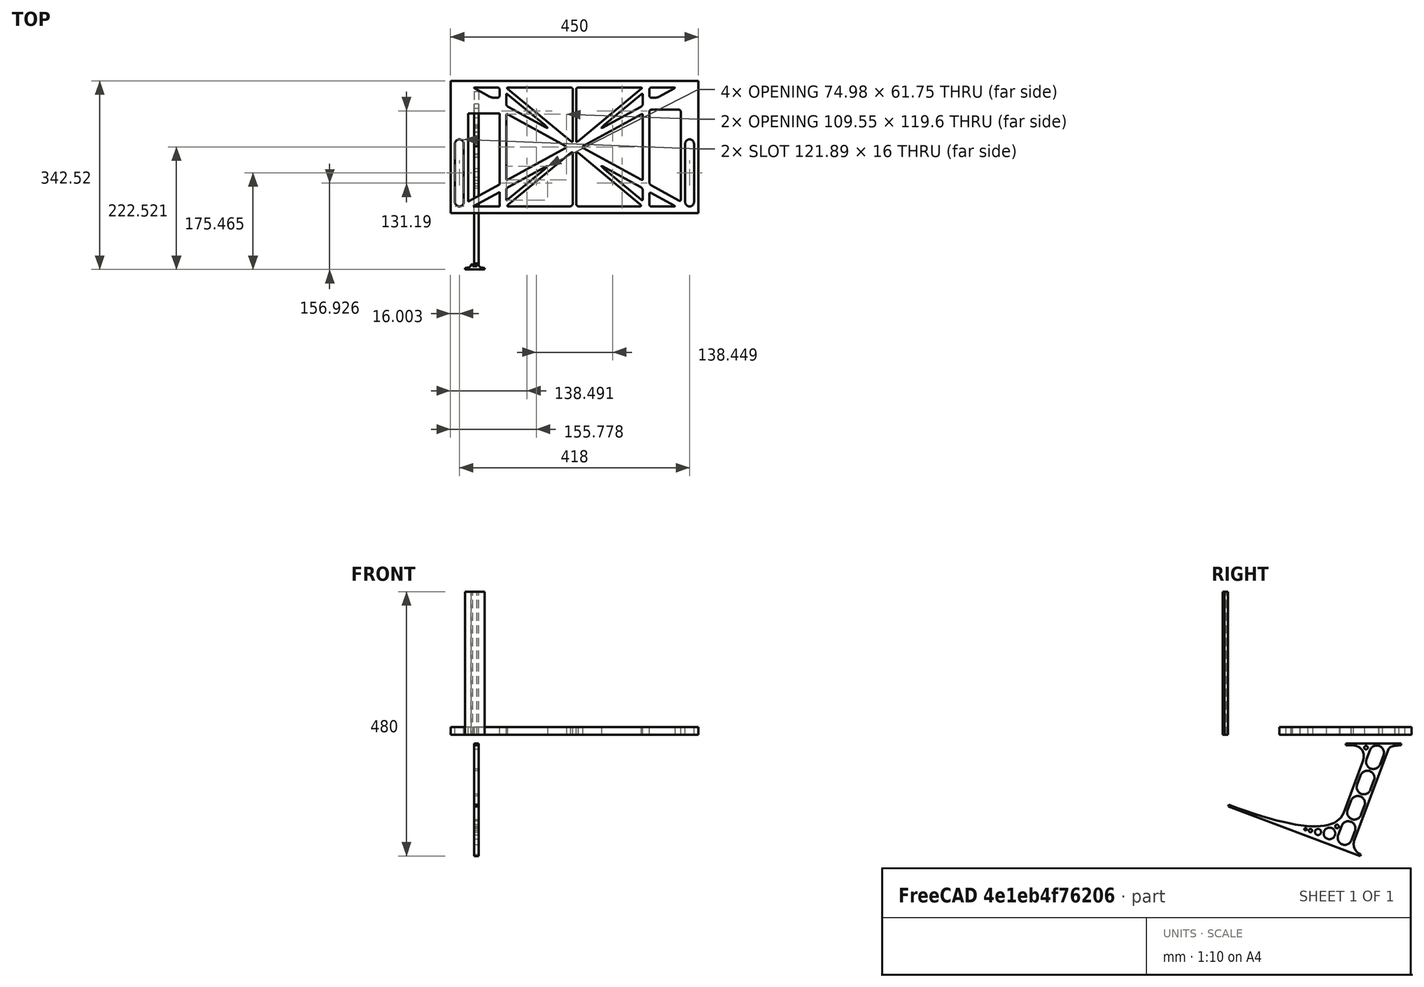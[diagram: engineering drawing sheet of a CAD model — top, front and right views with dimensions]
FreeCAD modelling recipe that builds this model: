
FCSTD DOCUMENT  (FreeCAD 0.19R0.19.2)
Label: laptopStand122FCStd
License: All rights reserved
LicenseURL: http://en.wikipedia.org/wiki/All_rights_reserved
objects: Sketcher::SketchObject×3, Part::Extrusion×3
note: 6 computed .brp shape members not serialized (recipe doc carries the construction recipe); baked Part::Feature solids carry a one-line shape summary decoded from their .brp

FEATURE [Sketcher::SketchObject] Sketch
  FullyConstrained = false
  sketch-geometry (338):
    g0: LineSegment StartX=-10.9272 StartY=-82.7794 StartZ=0 EndX=46.0728 EndY=-51.4823 EndZ=0
    g1: LineSegment StartX=-10.9272 StartY=77.3346 StartZ=0 EndX=-10.9272 EndY=-82.7794 EndZ=0
    g2: LineSegment StartX=46.0728 StartY=-65.424 StartZ=0 EndX=-1.92719 EndY=-91.7794 EndZ=0
    g3: LineSegment StartX=46.0728 StartY=-65.424 StartZ=0 EndX=46.0728 EndY=-91.7794 EndZ=0
    g4: LineSegment StartX=46.0728 StartY=77.3346 StartZ=0 EndX=46.0728 EndY=-51.4823 EndZ=0
    g5: LineSegment StartX=-42.9272 StartY=136.221 StartZ=0 EndX=-42.9272 EndY=-103.779 EndZ=0
    g6: LineSegment StartX=407.073 StartY=136.221 StartZ=0 EndX=407.073 EndY=-103.779 EndZ=0
    g7: ArcOfCircle CenterX=-26.9272 CenterY=22.1087 CenterZ=0 NormalX=0 NormalY=0 NormalZ=1 AngleXU=0 Radius=8 StartAngle=1e-16 EndAngle=3.14159
    g8: ArcOfCircle CenterX=-26.9272 CenterY=-83.7794 CenterZ=0 NormalX=0 NormalY=0 NormalZ=1 AngleXU=0 Radius=8 StartAngle=3.14159 EndAngle=6.28319
    g9: LineSegment StartX=-34.9272 StartY=22.1087 StartZ=0 EndX=-34.9272 EndY=-83.7794 EndZ=0
    g10: LineSegment StartX=-18.9272 StartY=22.1087 StartZ=0 EndX=-18.9272 EndY=-83.7794 EndZ=0
    g11: ArcOfCircle CenterX=391.073 CenterY=22.1087 CenterZ=0 NormalX=0 NormalY=0 NormalZ=1 AngleXU=0 Radius=8 StartAngle=-4.4e-15 EndAngle=3.14159
    g12: LineSegment StartX=399.073 StartY=22.1087 StartZ=0 EndX=399.073 EndY=-83.7794 EndZ=0
    g13: LineSegment StartX=383.073 StartY=22.1087 StartZ=0 EndX=383.073 EndY=-83.7794 EndZ=0
    g14: ArcOfCircle CenterX=391.073 CenterY=-83.7794 CenterZ=0 NormalX=0 NormalY=0 NormalZ=1 AngleXU=0 Radius=8 StartAngle=3.14159 EndAngle=6.28319
    g15: Circle CenterX=175.022 CenterY=27.0628 CenterZ=0 NormalX=0 NormalY=0 NormalZ=1 AngleXU=0 Radius=1
    g16: Circle CenterX=179.022 CenterY=24.8665 CenterZ=0 NormalX=0 NormalY=0 NormalZ=1 AngleXU=0 Radius=1
    g17: Circle CenterX=179.022 CenterY=27.0628 CenterZ=0 NormalX=0 NormalY=0 NormalZ=1 AngleXU=0 Radius=1
    g18: BSplineCurve PolesCount=3 KnotsCount=2 Degree=2 IsPeriodic=0
    g19: GeomPoint X=175.022 Y=27.0628 Z=0
    g20: GeomPoint X=179.022 Y=27.0628 Z=0
    g21: Circle CenterX=189.124 CenterY=27.0628 CenterZ=0 NormalX=0 NormalY=0 NormalZ=1 AngleXU=0 Radius=1
    g22: Circle CenterX=185.124 CenterY=24.8665 CenterZ=0 NormalX=0 NormalY=0 NormalZ=1 AngleXU=0 Radius=1
    g23: Circle CenterX=185.124 CenterY=27.0628 CenterZ=0 NormalX=0 NormalY=0 NormalZ=1 AngleXU=0 Radius=1
    g24: BSplineCurve PolesCount=3 KnotsCount=2 Degree=2 IsPeriodic=0
    g25: GeomPoint X=189.124 Y=27.0628 Z=0
    g26: GeomPoint X=185.124 Y=27.0628 Z=0
    g27: Circle CenterX=175.022 CenterY=5.37834 CenterZ=0 NormalX=0 NormalY=0 NormalZ=1 AngleXU=0 Radius=1
    g28: Circle CenterX=179.022 CenterY=7.57463 CenterZ=0 NormalX=0 NormalY=0 NormalZ=1 AngleXU=0 Radius=1
    g29: Circle CenterX=179.022 CenterY=5.34704 CenterZ=0 NormalX=0 NormalY=0 NormalZ=1 AngleXU=0 Radius=1
    g30: BSplineCurve PolesCount=3 KnotsCount=2 Degree=2 IsPeriodic=0
    g31: GeomPoint X=175.022 Y=5.37834 Z=0
    g32: GeomPoint X=179.022 Y=5.34704 Z=0
    g33: Circle CenterX=189.124 CenterY=5.37834 CenterZ=0 NormalX=0 NormalY=0 NormalZ=1 AngleXU=0 Radius=1
    g34: Circle CenterX=185.124 CenterY=7.57463 CenterZ=0 NormalX=0 NormalY=0 NormalZ=1 AngleXU=0 Radius=1
    g35: Circle CenterX=185.124 CenterY=5.34704 CenterZ=0 NormalX=0 NormalY=0 NormalZ=1 AngleXU=0 Radius=1
    g36: BSplineCurve PolesCount=3 KnotsCount=2 Degree=2 IsPeriodic=0
    g37: GeomPoint X=189.124 Y=5.37834 Z=0
    g38: GeomPoint X=185.124 Y=5.34704 Z=0
    g39: Circle CenterX=165.871 CenterY=18.1458 CenterZ=0 NormalX=0 NormalY=0 NormalZ=1 AngleXU=0 Radius=1
    g40: Circle CenterX=169.377 CenterY=16.2206 CenterZ=0 NormalX=0 NormalY=0 NormalZ=1 AngleXU=0 Radius=1
    g41: Circle CenterX=165.871 CenterY=14.2954 CenterZ=0 NormalX=0 NormalY=0 NormalZ=1 AngleXU=0 Radius=1
    g42: BSplineCurve PolesCount=3 KnotsCount=2 Degree=2 IsPeriodic=0
    g43: GeomPoint X=165.871 Y=18.1458 Z=0
    g44: GeomPoint X=165.871 Y=14.2954 Z=0
    g45: Circle CenterX=198.275 CenterY=18.1458 CenterZ=0 NormalX=0 NormalY=0 NormalZ=1 AngleXU=0 Radius=1
    g46: Circle CenterX=194.768 CenterY=16.2206 CenterZ=0 NormalX=0 NormalY=0 NormalZ=1 AngleXU=0 Radius=1
    g47: Circle CenterX=198.275 CenterY=14.2954 CenterZ=0 NormalX=0 NormalY=0 NormalZ=1 AngleXU=0 Radius=1
    g48: BSplineCurve PolesCount=3 KnotsCount=2 Degree=2 IsPeriodic=0
    g49: GeomPoint X=198.275 Y=18.1458 Z=0
    g50: GeomPoint X=198.275 Y=14.2954 Z=0
    g51: LineSegment StartX=407.073 StartY=-103.779 StartZ=0 EndX=-42.9272 EndY=-103.779 EndZ=0
    g52: LineSegment StartX=407.073 StartY=136.221 StartZ=0 EndX=-42.9272 EndY=136.221 EndZ=0
    g53: LineSegment StartX=46.0728 StartY=77.3346 StartZ=0 EndX=-10.9272 EndY=77.3346 EndZ=0
    g54: Circle CenterX=125.607 CenterY=54.1951 CenterZ=0 NormalX=0 NormalY=0 NormalZ=1 AngleXU=0 Radius=1
    g55: Circle CenterX=139.632 CenterY=46.4944 CenterZ=0 NormalX=0 NormalY=0 NormalZ=1 AngleXU=0 Radius=1
    g56: Circle CenterX=127.326 CenterY=56.7187 CenterZ=0 NormalX=0 NormalY=0 NormalZ=1 AngleXU=0 Radius=1
    g57: BSplineCurve PolesCount=3 KnotsCount=2 Degree=2 IsPeriodic=0
    g58: GeomPoint X=125.607 Y=54.1951 Z=0
    g59: GeomPoint X=127.326 Y=56.7187 Z=0
    g60: Circle CenterX=236.821 CenterY=56.7187 CenterZ=0 NormalX=0 NormalY=0 NormalZ=1 AngleXU=0 Radius=1
    g61: Circle CenterX=224.513 CenterY=46.4944 CenterZ=0 NormalX=0 NormalY=0 NormalZ=1 AngleXU=0 Radius=1
    g62: Circle CenterX=238.538 CenterY=54.1951 CenterZ=0 NormalX=0 NormalY=0 NormalZ=1 AngleXU=0 Radius=1
    g63: BSplineCurve PolesCount=3 KnotsCount=2 Degree=2 IsPeriodic=0
    g64: GeomPoint X=236.821 Y=56.7187 Z=0
    g65: GeomPoint X=238.538 Y=54.1951 Z=0
    g66: Circle CenterX=238.538 CenterY=-21.7539 CenterZ=0 NormalX=0 NormalY=0 NormalZ=1 AngleXU=0 Radius=1
    g67: Circle CenterX=224.513 CenterY=-14.0532 CenterZ=0 NormalX=0 NormalY=0 NormalZ=1 AngleXU=0 Radius=1
    g68: Circle CenterX=236.821 CenterY=-24.2775 CenterZ=0 NormalX=0 NormalY=0 NormalZ=1 AngleXU=0 Radius=1
    g69: BSplineCurve PolesCount=3 KnotsCount=2 Degree=2 IsPeriodic=0
    g70: GeomPoint X=238.538 Y=-21.7539 Z=0
    g71: GeomPoint X=236.821 Y=-24.2775 Z=0
    g72: Circle CenterX=125.607 CenterY=-21.7539 CenterZ=0 NormalX=0 NormalY=0 NormalZ=1 AngleXU=0 Radius=1
    g73: Circle CenterX=139.632 CenterY=-14.0532 CenterZ=0 NormalX=0 NormalY=0 NormalZ=1 AngleXU=0 Radius=1
    g74: Circle CenterX=127.325 CenterY=-24.2775 CenterZ=0 NormalX=0 NormalY=0 NormalZ=1 AngleXU=0 Radius=1
    g75: BSplineCurve PolesCount=3 KnotsCount=2 Degree=2 IsPeriodic=0
    g76: GeomPoint X=125.607 Y=-21.7539 Z=0
    g77: GeomPoint X=127.325 Y=-24.2775 Z=0
    g78: Circle CenterX=302.996 CenterY=111.695 CenterZ=0 NormalX=0 NormalY=0 NormalZ=1 AngleXU=0 Radius=1
    g79: Circle CenterX=306.073 CenterY=114.251 CenterZ=0 NormalX=0 NormalY=0 NormalZ=1 AngleXU=0 Radius=1
    g80: Circle CenterX=306.073 CenterY=110.251 CenterZ=0 NormalX=0 NormalY=0 NormalZ=1 AngleXU=0 Radius=1
    g81: BSplineCurve PolesCount=3 KnotsCount=2 Degree=2 IsPeriodic=0
    g82: GeomPoint X=302.996 Y=111.695 Z=0
    g83: GeomPoint X=306.073 Y=110.251 Z=0
    g84: Circle CenterX=306.073 CenterY=95.2763 CenterZ=0 NormalX=0 NormalY=0 NormalZ=1 AngleXU=0 Radius=1
    g85: Circle CenterX=306.073 CenterY=91.2763 CenterZ=0 NormalX=0 NormalY=0 NormalZ=1 AngleXU=0 Radius=1
    g86: Circle CenterX=302.567 CenterY=89.3511 CenterZ=0 NormalX=0 NormalY=0 NormalZ=1 AngleXU=0 Radius=1
    g87: BSplineCurve PolesCount=3 KnotsCount=2 Degree=2 IsPeriodic=0
    g88: GeomPoint X=306.073 Y=95.2763 Z=0
    g89: GeomPoint X=302.567 Y=89.3511 Z=0
    g90: LineSegment StartX=306.073 StartY=110.251 StartZ=0 EndX=306.073 EndY=95.2763 EndZ=0
    g91: LineSegment StartX=302.996 StartY=111.695 StartZ=0 EndX=236.821 EndY=56.7187 EndZ=0
    g92: LineSegment StartX=238.538 StartY=54.1951 StartZ=0 EndX=302.567 EndY=89.3511 EndZ=0
    g93: Circle CenterX=61.1496 CenterY=111.695 CenterZ=0 NormalX=0 NormalY=0 NormalZ=1 AngleXU=0 Radius=1
    g94: Circle CenterX=58.0728 CenterY=114.251 CenterZ=0 NormalX=0 NormalY=0 NormalZ=1 AngleXU=0 Radius=1
    g95: Circle CenterX=58.0728 CenterY=110.251 CenterZ=0 NormalX=0 NormalY=0 NormalZ=1 AngleXU=0 Radius=1
    g96: BSplineCurve PolesCount=3 KnotsCount=2 Degree=2 IsPeriodic=0
    g97: GeomPoint X=61.1496 Y=111.695 Z=0
    g98: GeomPoint X=58.0728 Y=110.251 Z=0
    g99: Circle CenterX=61.5791 CenterY=89.3511 CenterZ=0 NormalX=0 NormalY=0 NormalZ=1 AngleXU=0 Radius=1
    g100: Circle CenterX=58.0728 CenterY=91.2763 CenterZ=0 NormalX=0 NormalY=0 NormalZ=1 AngleXU=0 Radius=1
    g101: Circle CenterX=58.0728 CenterY=95.2763 CenterZ=0 NormalX=0 NormalY=0 NormalZ=1 AngleXU=0 Radius=1
    g102: BSplineCurve PolesCount=3 KnotsCount=2 Degree=2 IsPeriodic=0
    g103: GeomPoint X=61.5791 Y=89.3511 Z=0
    g104: GeomPoint X=58.0728 Y=95.2763 Z=0
    g105: LineSegment StartX=58.0728 StartY=110.251 StartZ=0 EndX=58.0728 EndY=95.2763 EndZ=0
    g106: LineSegment StartX=61.1496 StartY=111.695 StartZ=0 EndX=127.326 EndY=56.7187 EndZ=0
    g107: LineSegment StartX=125.607 StartY=54.1951 StartZ=0 EndX=61.5791 EndY=89.3511 EndZ=0
    g108: Circle CenterX=61.5791 CenterY=-56.9099 CenterZ=0 NormalX=0 NormalY=0 NormalZ=1 AngleXU=0 Radius=1
    g109: Circle CenterX=58.0728 CenterY=-58.8351 CenterZ=0 NormalX=0 NormalY=0 NormalZ=1 AngleXU=0 Radius=1
    g110: Circle CenterX=58.0728 CenterY=-62.8351 CenterZ=0 NormalX=0 NormalY=0 NormalZ=1 AngleXU=0 Radius=1
    g111: BSplineCurve PolesCount=3 KnotsCount=2 Degree=2 IsPeriodic=0
    g112: GeomPoint X=61.5791 Y=-56.9099 Z=0
    g113: GeomPoint X=58.0728 Y=-62.8351 Z=0
    g114: Circle CenterX=58.0728 CenterY=-77.8102 CenterZ=0 NormalX=0 NormalY=0 NormalZ=1 AngleXU=0 Radius=1
    g115: Circle CenterX=58.0728 CenterY=-81.8102 CenterZ=0 NormalX=0 NormalY=0 NormalZ=1 AngleXU=0 Radius=1
    g116: Circle CenterX=61.1496 CenterY=-79.2541 CenterZ=0 NormalX=0 NormalY=0 NormalZ=1 AngleXU=0 Radius=1
    g117: BSplineCurve PolesCount=3 KnotsCount=2 Degree=2 IsPeriodic=0
    g118: GeomPoint X=58.0728 Y=-77.8102 Z=0
    g119: GeomPoint X=61.1496 Y=-79.2541 Z=0
    g120: LineSegment StartX=58.0728 StartY=-62.8351 StartZ=0 EndX=58.0728 EndY=-77.8102 EndZ=0
    g121: LineSegment StartX=61.1496 StartY=-79.2541 StartZ=0 EndX=127.325 EndY=-24.2775 EndZ=0
    g122: LineSegment StartX=125.607 StartY=-21.7539 StartZ=0 EndX=61.5791 EndY=-56.9099 EndZ=0
    g123: Circle CenterX=302.567 CenterY=-56.9099 CenterZ=0 NormalX=0 NormalY=0 NormalZ=1 AngleXU=0 Radius=1
    g124: Circle CenterX=306.073 CenterY=-58.8351 CenterZ=0 NormalX=0 NormalY=0 NormalZ=1 AngleXU=0 Radius=1
    g125: Circle CenterX=306.073 CenterY=-62.8351 CenterZ=0 NormalX=0 NormalY=0 NormalZ=1 AngleXU=0 Radius=1
    g126: BSplineCurve PolesCount=3 KnotsCount=2 Degree=2 IsPeriodic=0
    g127: GeomPoint X=302.567 Y=-56.9099 Z=0
    g128: GeomPoint X=306.073 Y=-62.8351 Z=0
    g129: Circle CenterX=302.996 CenterY=-79.2541 CenterZ=0 NormalX=0 NormalY=0 NormalZ=1 AngleXU=0 Radius=1
    g130: Circle CenterX=306.073 CenterY=-81.8102 CenterZ=0 NormalX=0 NormalY=0 NormalZ=1 AngleXU=0 Radius=1
    g131: Circle CenterX=306.073 CenterY=-77.8102 CenterZ=0 NormalX=0 NormalY=0 NormalZ=1 AngleXU=0 Radius=1
    g132: BSplineCurve PolesCount=3 KnotsCount=2 Degree=2 IsPeriodic=0
    g133: GeomPoint X=302.996 Y=-79.2541 Z=0
    g134: GeomPoint X=306.073 Y=-77.8102 Z=0
    g135: LineSegment StartX=306.073 StartY=-62.8351 StartZ=0 EndX=306.073 EndY=-77.8102 EndZ=0
    g136: LineSegment StartX=302.996 StartY=-79.2541 StartZ=0 EndX=236.821 EndY=-24.2775 EndZ=0
    g137: LineSegment StartX=238.538 StartY=-21.7539 StartZ=0 EndX=302.567 EndY=-56.9099 EndZ=0
    g138: Circle CenterX=61.6457 CenterY=-88.8112 CenterZ=0 NormalX=0 NormalY=0 NormalZ=1 AngleXU=0 Radius=1
    g139: Circle CenterX=58.0728 CenterY=-91.7794 CenterZ=0 NormalX=0 NormalY=0 NormalZ=1 AngleXU=0 Radius=1
    g140: Circle CenterX=63.9135 CenterY=-91.7794 CenterZ=0 NormalX=0 NormalY=0 NormalZ=1 AngleXU=0 Radius=1
    g141: BSplineCurve PolesCount=3 KnotsCount=2 Degree=2 IsPeriodic=0
    g142: GeomPoint X=61.6457 Y=-88.8112 Z=0
    g143: GeomPoint X=63.9135 Y=-91.7794 Z=0
    g144: Circle CenterX=179.022 CenterY=-85.8163 CenterZ=0 NormalX=0 NormalY=0 NormalZ=1 AngleXU=0 Radius=1
    g145: Circle CenterX=179.022 CenterY=-91.7794 CenterZ=0 NormalX=0 NormalY=0 NormalZ=1 AngleXU=0 Radius=1
    g146: Circle CenterX=171.895 CenterY=-91.7794 CenterZ=0 NormalX=0 NormalY=0 NormalZ=1 AngleXU=0 Radius=1
    g147: BSplineCurve PolesCount=3 KnotsCount=2 Degree=2 IsPeriodic=0
    g148: GeomPoint X=179.022 Y=-85.8163 Z=0
    g149: GeomPoint X=171.895 Y=-91.7794 Z=0
    g150: Circle CenterX=185.124 CenterY=-86.2028 CenterZ=0 NormalX=0 NormalY=0 NormalZ=1 AngleXU=0 Radius=1
    g151: Circle CenterX=185.124 CenterY=-91.7794 CenterZ=0 NormalX=0 NormalY=0 NormalZ=1 AngleXU=0 Radius=1
    g152: Circle CenterX=191.747 CenterY=-91.7794 CenterZ=0 NormalX=0 NormalY=0 NormalZ=1 AngleXU=0 Radius=1
    g153: BSplineCurve PolesCount=3 KnotsCount=2 Degree=2 IsPeriodic=0
    g154: GeomPoint X=185.124 Y=-86.2028 Z=0
    g155: GeomPoint X=191.747 Y=-91.7794 Z=0
    g156: Circle CenterX=299.888 CenterY=-86.6413 CenterZ=0 NormalX=0 NormalY=0 NormalZ=1 AngleXU=0 Radius=1
    g157: Circle CenterX=306.073 CenterY=-91.7794 CenterZ=0 NormalX=0 NormalY=0 NormalZ=1 AngleXU=0 Radius=1
    g158: Circle CenterX=298.776 CenterY=-91.7794 CenterZ=0 NormalX=0 NormalY=0 NormalZ=1 AngleXU=0 Radius=1
    g159: BSplineCurve PolesCount=3 KnotsCount=2 Degree=2 IsPeriodic=0
    g160: GeomPoint X=299.888 Y=-86.6413 Z=0
    g161: GeomPoint X=298.776 Y=-91.7794 Z=0
    g162: LineSegment StartX=189.124 StartY=5.37834 StartZ=0 EndX=299.888 EndY=-86.6413 EndZ=0
    g163: LineSegment StartX=298.776 StartY=-91.7794 StartZ=0 EndX=191.747 EndY=-91.7794 EndZ=0
    g164: LineSegment StartX=185.124 StartY=-86.2028 StartZ=0 EndX=185.124 EndY=5.34704 EndZ=0
    g165: LineSegment StartX=179.022 StartY=5.34704 StartZ=0 EndX=179.022 EndY=-85.8163 EndZ=0
    g166: LineSegment StartX=171.895 StartY=-91.7794 StartZ=0 EndX=63.9135 EndY=-91.7794 EndZ=0
    g167: LineSegment StartX=61.6457 StartY=-88.8112 StartZ=0 EndX=175.022 EndY=5.37834 EndZ=0
    g168: Circle CenterX=302.073 CenterY=124.221 CenterZ=0 NormalX=0 NormalY=0 NormalZ=1 AngleXU=0 Radius=1
    g169: Circle CenterX=306.073 CenterY=124.221 CenterZ=0 NormalX=0 NormalY=0 NormalZ=1 AngleXU=0 Radius=1
    g170: Circle CenterX=302.996 CenterY=121.665 CenterZ=0 NormalX=0 NormalY=0 NormalZ=1 AngleXU=0 Radius=1
    g171: BSplineCurve PolesCount=3 KnotsCount=2 Degree=2 IsPeriodic=0
    g172: GeomPoint X=302.073 Y=124.221 Z=0
    g173: GeomPoint X=302.996 Y=121.665 Z=0
    g174: Circle CenterX=189.124 CenterY=124.221 CenterZ=0 NormalX=0 NormalY=0 NormalZ=1 AngleXU=0 Radius=1
    g175: Circle CenterX=185.124 CenterY=124.221 CenterZ=0 NormalX=0 NormalY=0 NormalZ=1 AngleXU=0 Radius=1
    g176: Circle CenterX=185.124 CenterY=120.221 CenterZ=0 NormalX=0 NormalY=0 NormalZ=1 AngleXU=0 Radius=1
    g177: BSplineCurve PolesCount=3 KnotsCount=2 Degree=2 IsPeriodic=0
    g178: GeomPoint X=189.124 Y=124.221 Z=0
    g179: GeomPoint X=185.124 Y=120.221 Z=0
    g180: Circle CenterX=175.022 CenterY=124.221 CenterZ=0 NormalX=0 NormalY=0 NormalZ=1 AngleXU=0 Radius=1
    g181: Circle CenterX=179.022 CenterY=124.221 CenterZ=0 NormalX=0 NormalY=0 NormalZ=1 AngleXU=0 Radius=1
    g182: Circle CenterX=179.022 CenterY=120.221 CenterZ=0 NormalX=0 NormalY=0 NormalZ=1 AngleXU=0 Radius=1
    g183: BSplineCurve PolesCount=3 KnotsCount=2 Degree=2 IsPeriodic=0
    g184: GeomPoint X=175.022 Y=124.221 Z=0
    g185: GeomPoint X=179.022 Y=120.221 Z=0
    g186: Circle CenterX=62.0728 CenterY=124.221 CenterZ=0 NormalX=0 NormalY=0 NormalZ=1 AngleXU=0 Radius=1
    g187: Circle CenterX=58.0728 CenterY=124.221 CenterZ=0 NormalX=0 NormalY=0 NormalZ=1 AngleXU=0 Radius=1
    g188: Circle CenterX=61.1496 CenterY=121.665 CenterZ=0 NormalX=0 NormalY=0 NormalZ=1 AngleXU=0 Radius=1
    g189: BSplineCurve PolesCount=3 KnotsCount=2 Degree=2 IsPeriodic=0
    g190: GeomPoint X=62.0728 Y=124.221 Z=0
    g191: GeomPoint X=61.1496 Y=121.665 Z=0
    g192: LineSegment StartX=62.0728 StartY=124.221 StartZ=0 EndX=175.022 EndY=124.221 EndZ=0
    g193: LineSegment StartX=179.022 StartY=120.221 StartZ=0 EndX=179.022 EndY=27.0628 EndZ=0
    g194: LineSegment StartX=185.124 StartY=27.0628 StartZ=0 EndX=185.124 EndY=120.221 EndZ=0
    g195: LineSegment StartX=189.124 StartY=124.221 StartZ=0 EndX=302.073 EndY=124.221 EndZ=0
    g196: LineSegment StartX=302.996 StartY=121.665 StartZ=0 EndX=189.124 EndY=27.0628 EndZ=0
    g197: LineSegment StartX=175.022 StartY=27.0628 StartZ=0 EndX=61.1496 EndY=121.665 EndZ=0
    g198: Circle CenterX=61.5791 CenterY=75.4095 CenterZ=0 NormalX=0 NormalY=0 NormalZ=1 AngleXU=0 Radius=1
    g199: Circle CenterX=58.0728 CenterY=77.3346 CenterZ=0 NormalX=0 NormalY=0 NormalZ=1 AngleXU=0 Radius=1
    g200: Circle CenterX=58.0728 CenterY=73.3346 CenterZ=0 NormalX=0 NormalY=0 NormalZ=1 AngleXU=0 Radius=1
    g201: BSplineCurve PolesCount=3 KnotsCount=2 Degree=2 IsPeriodic=0
    g202: GeomPoint X=61.5791 Y=75.4095 Z=0
    g203: GeomPoint X=58.0728 Y=73.3346 Z=0
    g204: Circle CenterX=58.0728 CenterY=-40.8935 CenterZ=0 NormalX=0 NormalY=0 NormalZ=1 AngleXU=0 Radius=1
    g205: Circle CenterX=58.0728 CenterY=-44.8935 CenterZ=0 NormalX=0 NormalY=0 NormalZ=1 AngleXU=0 Radius=1
    g206: Circle CenterX=61.5791 CenterY=-42.9683 CenterZ=0 NormalX=0 NormalY=0 NormalZ=1 AngleXU=0 Radius=1
    g207: BSplineCurve PolesCount=3 KnotsCount=2 Degree=2 IsPeriodic=0
    g208: GeomPoint X=58.0728 Y=-40.8935 Z=0
    g209: GeomPoint X=61.5791 Y=-42.9683 Z=0
    g210: LineSegment StartX=61.5791 StartY=-42.9683 StartZ=0 EndX=165.871 EndY=14.2954 EndZ=0
    g211: LineSegment StartX=165.871 StartY=18.1458 StartZ=0 EndX=61.5791 EndY=75.4095 EndZ=0
    g212: LineSegment StartX=58.0728 StartY=73.3346 StartZ=0 EndX=58.0728 EndY=-40.8935 EndZ=0
    g213: Circle CenterX=302.567 CenterY=-42.9683 CenterZ=0 NormalX=0 NormalY=0 NormalZ=1 AngleXU=0 Radius=1
    g214: Circle CenterX=306.073 CenterY=-44.8935 CenterZ=0 NormalX=0 NormalY=0 NormalZ=1 AngleXU=0 Radius=1
    g215: Circle CenterX=306.073 CenterY=-40.8935 CenterZ=0 NormalX=0 NormalY=0 NormalZ=1 AngleXU=0 Radius=1
    g216: BSplineCurve PolesCount=3 KnotsCount=2 Degree=2 IsPeriodic=0
    g217: GeomPoint X=302.567 Y=-42.9683 Z=0
    g218: GeomPoint X=306.073 Y=-40.8935 Z=0
    g219: Circle CenterX=306.073 CenterY=73.3346 CenterZ=0 NormalX=0 NormalY=0 NormalZ=1 AngleXU=0 Radius=1
    g220: Circle CenterX=306.073 CenterY=77.3346 CenterZ=0 NormalX=0 NormalY=0 NormalZ=1 AngleXU=0 Radius=1
    g221: Circle CenterX=302.567 CenterY=75.4095 CenterZ=0 NormalX=0 NormalY=0 NormalZ=1 AngleXU=0 Radius=1
    g222: BSplineCurve PolesCount=3 KnotsCount=2 Degree=2 IsPeriodic=0
    g223: GeomPoint X=306.073 Y=73.3346 Z=0
    g224: GeomPoint X=302.567 Y=75.4095 Z=0
    g225: LineSegment StartX=302.567 StartY=-42.9683 StartZ=0 EndX=198.275 EndY=14.2954 EndZ=0
    g226: LineSegment StartX=198.275 StartY=18.1458 StartZ=0 EndX=302.567 EndY=75.4095 EndZ=0
    g227: LineSegment StartX=306.073 StartY=73.3346 StartZ=0 EndX=306.073 EndY=-40.8935 EndZ=0
    g228: LineSegment StartX=322.073 StartY=105.865 StartZ=0 EndX=328.643 EndY=105.865 EndZ=0
    g229: LineSegment StartX=318.073 StartY=120.221 StartZ=0 EndX=318.073 EndY=109.865 EndZ=0
    g230: LineSegment StartX=336.157 StartY=107.779 StartZ=0 EndX=362.567 EndY=122.294 EndZ=0
    g231: Circle CenterX=362.073 CenterY=124.221 CenterZ=0 NormalX=0 NormalY=0 NormalZ=1 AngleXU=0 Radius=1
    g232: Circle CenterX=366.073 CenterY=124.221 CenterZ=0 NormalX=0 NormalY=0 NormalZ=1 AngleXU=0 Radius=1
    g233: Circle CenterX=362.567 CenterY=122.294 CenterZ=0 NormalX=0 NormalY=0 NormalZ=1 AngleXU=0 Radius=1
    g234: BSplineCurve PolesCount=3 KnotsCount=2 Degree=2 IsPeriodic=0
    g235: GeomPoint X=362.073 Y=124.221 Z=0
    g236: GeomPoint X=362.567 Y=122.294 Z=0
    g237: Circle CenterX=322.073 CenterY=124.221 CenterZ=0 NormalX=0 NormalY=0 NormalZ=1 AngleXU=0 Radius=1
    g238: Circle CenterX=318.073 CenterY=124.221 CenterZ=0 NormalX=0 NormalY=0 NormalZ=1 AngleXU=0 Radius=1
    g239: Circle CenterX=318.073 CenterY=120.221 CenterZ=0 NormalX=0 NormalY=0 NormalZ=1 AngleXU=0 Radius=1
    g240: BSplineCurve PolesCount=3 KnotsCount=2 Degree=2 IsPeriodic=0
    g241: GeomPoint X=322.073 Y=124.221 Z=0
    g242: GeomPoint X=318.073 Y=120.221 Z=0
    g243: Circle CenterX=322.073 CenterY=105.865 CenterZ=0 NormalX=0 NormalY=0 NormalZ=1 AngleXU=0 Radius=1
    g244: Circle CenterX=318.073 CenterY=105.865 CenterZ=0 NormalX=0 NormalY=0 NormalZ=1 AngleXU=0 Radius=1
    g245: Circle CenterX=318.073 CenterY=109.865 CenterZ=0 NormalX=0 NormalY=0 NormalZ=1 AngleXU=0 Radius=1
    g246: BSplineCurve PolesCount=3 KnotsCount=2 Degree=2 IsPeriodic=0
    g247: GeomPoint X=322.073 Y=105.865 Z=0
    g248: GeomPoint X=318.073 Y=109.865 Z=0
    g249: Circle CenterX=336.157 CenterY=107.779 CenterZ=0 NormalX=0 NormalY=0 NormalZ=1 AngleXU=0 Radius=1
    g250: Circle CenterX=332.651 CenterY=105.853 CenterZ=0 NormalX=0 NormalY=0 NormalZ=1 AngleXU=0 Radius=1
    g251: Circle CenterX=328.643 CenterY=105.865 CenterZ=0 NormalX=0 NormalY=0 NormalZ=1 AngleXU=0 Radius=1
    g252: BSplineCurve PolesCount=3 KnotsCount=2 Degree=2 IsPeriodic=0
    g253: GeomPoint X=336.157 Y=107.779 Z=0
    g254: GeomPoint X=328.643 Y=105.865 Z=0
    g255: LineSegment StartX=322.073 StartY=124.221 StartZ=0 EndX=362.073 EndY=124.221 EndZ=0
    g256: Circle CenterX=371.567 CenterY=-80.8644 CenterZ=0 NormalX=0 NormalY=0 NormalZ=1 AngleXU=0 Radius=1
    g257: Circle CenterX=375.073 CenterY=-82.7896 CenterZ=0 NormalX=0 NormalY=0 NormalZ=1 AngleXU=0 Radius=1
    g258: Circle CenterX=375.073 CenterY=-78.7896 CenterZ=0 NormalX=0 NormalY=0 NormalZ=1 AngleXU=0 Radius=1
    g259: BSplineCurve PolesCount=3 KnotsCount=2 Degree=2 IsPeriodic=0
    g260: GeomPoint X=371.567 Y=-80.8644 Z=0
    g261: GeomPoint X=375.073 Y=-78.7896 Z=0
    g262: Circle CenterX=321.579 CenterY=-53.4075 CenterZ=0 NormalX=0 NormalY=0 NormalZ=1 AngleXU=0 Radius=1
    g263: Circle CenterX=318.073 CenterY=-51.4823 CenterZ=0 NormalX=0 NormalY=0 NormalZ=1 AngleXU=0 Radius=1
    g264: Circle CenterX=318.073 CenterY=-47.4823 CenterZ=0 NormalX=0 NormalY=0 NormalZ=1 AngleXU=0 Radius=1
    g265: BSplineCurve PolesCount=3 KnotsCount=2 Degree=2 IsPeriodic=0
    g266: GeomPoint X=321.579 Y=-53.4075 Z=0
    g267: GeomPoint X=318.073 Y=-47.4823 Z=0
    g268: Circle CenterX=318.073 CenterY=79.9235 CenterZ=0 NormalX=0 NormalY=0 NormalZ=1 AngleXU=0 Radius=1
    g269: Circle CenterX=318.073 CenterY=83.9235 CenterZ=0 NormalX=0 NormalY=0 NormalZ=1 AngleXU=0 Radius=1
    g270: Circle CenterX=322.073 CenterY=83.9235 CenterZ=0 NormalX=0 NormalY=0 NormalZ=1 AngleXU=0 Radius=1
    g271: BSplineCurve PolesCount=3 KnotsCount=2 Degree=2 IsPeriodic=0
    g272: GeomPoint X=318.073 Y=79.9235 Z=0
    g273: GeomPoint X=322.073 Y=83.9235 Z=0
    g274: Circle CenterX=375.073 CenterY=79.9235 CenterZ=0 NormalX=0 NormalY=0 NormalZ=1 AngleXU=0 Radius=1
    g275: Circle CenterX=375.073 CenterY=83.9235 CenterZ=0 NormalX=0 NormalY=0 NormalZ=1 AngleXU=0 Radius=1
    g276: Circle CenterX=371.073 CenterY=83.9235 CenterZ=0 NormalX=0 NormalY=0 NormalZ=1 AngleXU=0 Radius=1
    g277: BSplineCurve PolesCount=3 KnotsCount=2 Degree=2 IsPeriodic=0
    g278: GeomPoint X=375.073 Y=79.9235 Z=0
    g279: GeomPoint X=371.073 Y=83.9235 Z=0
    g280: LineSegment StartX=322.073 StartY=83.9235 StartZ=0 EndX=371.073 EndY=83.9235 EndZ=0
    g281: LineSegment StartX=375.073 StartY=79.9235 StartZ=0 EndX=375.073 EndY=-78.7896 EndZ=0
    g282: LineSegment StartX=371.567 StartY=-80.8644 StartZ=0 EndX=321.579 EndY=-53.4075 EndZ=0
    g283: LineSegment StartX=318.073 StartY=-47.4823 StartZ=0 EndX=318.073 EndY=79.9235 EndZ=0
    g284: Circle CenterX=321.579 CenterY=-67.3492 CenterZ=0 NormalX=0 NormalY=0 NormalZ=1 AngleXU=0 Radius=1
    g285: Circle CenterX=318.073 CenterY=-65.424 CenterZ=0 NormalX=0 NormalY=0 NormalZ=1 AngleXU=0 Radius=1
    g286: Circle CenterX=318.073 CenterY=-69.424 CenterZ=0 NormalX=0 NormalY=0 NormalZ=1 AngleXU=0 Radius=1
    g287: BSplineCurve PolesCount=3 KnotsCount=2 Degree=2 IsPeriodic=0
    g288: GeomPoint X=321.579 Y=-67.3492 Z=0
    g289: GeomPoint X=318.073 Y=-69.424 Z=0
    g290: Circle CenterX=362.567 CenterY=-89.8542 CenterZ=0 NormalX=0 NormalY=0 NormalZ=1 AngleXU=0 Radius=1
    g291: Circle CenterX=366.073 CenterY=-91.7794 CenterZ=0 NormalX=0 NormalY=0 NormalZ=1 AngleXU=0 Radius=1
    g292: Circle CenterX=362.073 CenterY=-91.7794 CenterZ=0 NormalX=0 NormalY=0 NormalZ=1 AngleXU=0 Radius=1
    g293: BSplineCurve PolesCount=3 KnotsCount=2 Degree=2 IsPeriodic=0
    g294: GeomPoint X=362.567 Y=-89.8542 Z=0
    g295: GeomPoint X=362.073 Y=-91.7794 Z=0
    g296: Circle CenterX=322.073 CenterY=-91.7794 CenterZ=0 NormalX=0 NormalY=0 NormalZ=1 AngleXU=0 Radius=1
    g297: Circle CenterX=318.073 CenterY=-91.7794 CenterZ=0 NormalX=0 NormalY=0 NormalZ=1 AngleXU=0 Radius=1
    g298: Circle CenterX=318.073 CenterY=-87.7794 CenterZ=0 NormalX=0 NormalY=0 NormalZ=1 AngleXU=0 Radius=1
    g299: BSplineCurve PolesCount=3 KnotsCount=2 Degree=2 IsPeriodic=0
    g300: GeomPoint X=322.073 Y=-91.7794 Z=0
    g301: GeomPoint X=318.073 Y=-87.7794 Z=0
    g302: LineSegment StartX=362.567 StartY=-89.8542 StartZ=0 EndX=321.579 EndY=-67.3492 EndZ=0
    g303: LineSegment StartX=318.073 StartY=-69.424 StartZ=0 EndX=318.073 EndY=-87.7794 EndZ=0
    g304: LineSegment StartX=322.073 StartY=-91.7794 StartZ=0 EndX=362.073 EndY=-91.7794 EndZ=0
    g305: Circle CenterX=2.07281 CenterY=124.221 CenterZ=0 NormalX=0 NormalY=0 NormalZ=1 AngleXU=0 Radius=1
    g306: Circle CenterX=1.57905 CenterY=122.295 CenterZ=0 NormalX=0 NormalY=0 NormalZ=1 AngleXU=0 Radius=1
    g307: BSplineCurve PolesCount=3 KnotsCount=2 Degree=2 IsPeriodic=0
    g308: GeomPoint X=2.07281 Y=124.221 Z=0
    g309: GeomPoint X=1.57905 Y=122.295 Z=0
    g310: Circle CenterX=42.0728 CenterY=124.221 CenterZ=0 NormalX=0 NormalY=0 NormalZ=1 AngleXU=0 Radius=1
    g311: Circle CenterX=46.0728 CenterY=124.221 CenterZ=0 NormalX=0 NormalY=0 NormalZ=1 AngleXU=0 Radius=1
    g312: Circle CenterX=46.0728 CenterY=120.221 CenterZ=0 NormalX=0 NormalY=0 NormalZ=1 AngleXU=0 Radius=1
    g313: BSplineCurve PolesCount=3 KnotsCount=2 Degree=2 IsPeriodic=0
    g314: GeomPoint X=42.0728 Y=124.221 Z=0
    g315: GeomPoint X=46.0728 Y=120.221 Z=0
    g316: Circle CenterX=46.0728 CenterY=109.865 CenterZ=0 NormalX=0 NormalY=0 NormalZ=1 AngleXU=0 Radius=1
    g317: Circle CenterX=46.0728 CenterY=105.865 CenterZ=0 NormalX=0 NormalY=0 NormalZ=1 AngleXU=0 Radius=1
    g318: Circle CenterX=42.0728 CenterY=105.865 CenterZ=0 NormalX=0 NormalY=0 NormalZ=1 AngleXU=0 Radius=1
    g319: BSplineCurve PolesCount=3 KnotsCount=2 Degree=2 IsPeriodic=0
    g320: GeomPoint X=46.0728 Y=109.865 Z=0
    g321: GeomPoint X=42.0728 Y=105.865 Z=0
    g322: Circle CenterX=35.5028 CenterY=105.865 CenterZ=0 NormalX=0 NormalY=0 NormalZ=1 AngleXU=0 Radius=1
    g323: Circle CenterX=31.5028 CenterY=105.865 CenterZ=0 NormalX=0 NormalY=0 NormalZ=1 AngleXU=0 Radius=1
    g324: Circle CenterX=27.9965 CenterY=107.79 CenterZ=0 NormalX=0 NormalY=0 NormalZ=1 AngleXU=0 Radius=1
    g325: BSplineCurve PolesCount=3 KnotsCount=2 Degree=2 IsPeriodic=0
    g326: GeomPoint X=35.5028 Y=105.865 Z=0
    g327: GeomPoint X=27.9965 Y=107.79 Z=0
    g328: LineSegment StartX=2.07281 StartY=124.221 StartZ=0 EndX=42.0728 EndY=124.221 EndZ=0
    g329: LineSegment StartX=46.0728 StartY=120.221 StartZ=0 EndX=46.0728 EndY=109.865 EndZ=0
    g330: LineSegment StartX=42.0728 StartY=105.865 StartZ=0 EndX=35.5028 EndY=105.865 EndZ=0
    g331: LineSegment StartX=27.9965 StartY=107.79 StartZ=0 EndX=1.57905 EndY=122.295 EndZ=0
    g332: LineSegment StartX=46.0728 StartY=-65.424 StartZ=0 EndX=46.0728 EndY=-69.424 EndZ=0
    g333: LineSegment StartX=46.0728 StartY=-91.7794 StartZ=0 EndX=46.0728 EndY=-87.7794 EndZ=0
    g334: LineSegment StartX=46.0728 StartY=-91.7794 StartZ=0 EndX=42.0728 EndY=-91.7794 EndZ=0
    g335: LineSegment StartX=-1.92719 StartY=-91.7794 StartZ=0 EndX=2.07281 EndY=-91.7794 EndZ=0
    g336: LineSegment StartX=-1.92719 StartY=-91.7794 StartZ=0 EndX=1.57905 EndY=-89.8542 EndZ=0
    g337: LineSegment StartX=46.0728 StartY=-65.424 StartZ=0 EndX=42.5666 EndY=-67.3492 EndZ=0
  constraints (567):
    c: Coincident(g3,g2)
    c: Coincident(g0,g4)
    c: Block(g3)
    c: Block(g2)
    c: Block(g0)
    c: Block(g1)
    c: Vertical(g5)
    c: Vertical(g6)
    c: Block(g6)
    c: Block(g5)
    c: Tangent(g7,g10) = 1.5708
    c: Tangent(g7,g9) = -1.5708
    c: Tangent(g9,g8) = -1.5708
    c: Tangent(g10,g8) = 1.5708
    c: Vertical(g9)
    c: Equal(g7,g8)
    c: Block(g10)
    c: Block(g9)
    c: Tangent(g11,g12) = 1.5708
    c: Tangent(g12,g14) = 1.5708
    c: Equal(g11,g14)
    c: Coincident(g13,g11)
    c: Coincident(g13,g14)
    c: Block(g12)
    c: Block(g13)
    c: Weight(g15) = 1
    c: Equal(g15,g16)
    c: Equal(g15,g17)
    c: InternalAlignment(g15,g18)
    c: InternalAlignment(g16,g18)
    c: InternalAlignment(g17,g18)
    c: InternalAlignment(g19,g18)
    c: InternalAlignment(g20,g18)
    c: Weight(g21) = 1
    c: Equal(g21,g22)
    c: Equal(g21,g23)
    c: InternalAlignment(g21,g24)
    c: InternalAlignment(g22,g24)
    c: InternalAlignment(g23,g24)
    c: InternalAlignment(g25,g24)
    c: InternalAlignment(g26,g24)
    c: Block(g24)
    c: Block(g18)
    c: Weight(g27) = 1
    c: Equal(g27,g28)
    c: Equal(g27,g29)
    c: InternalAlignment(g27,g30)
    c: InternalAlignment(g28,g30)
    c: InternalAlignment(g29,g30)
    c: InternalAlignment(g31,g30)
    c: InternalAlignment(g32,g30)
    c: Weight(g33) = 1
    c: Equal(g33,g34)
    c: Equal(g33,g35)
    c: InternalAlignment(g33,g36)
    c: InternalAlignment(g34,g36)
    c: InternalAlignment(g35,g36)
    c: InternalAlignment(g37,g36)
    c: InternalAlignment(g38,g36)
    c: Block(g36)
    c: Block(g30)
    c: Weight(g39) = 1
    c: Equal(g39,g40)
    c: Equal(g39,g41)
    c: InternalAlignment(g39,g42)
    c: InternalAlignment(g40,g42)
    c: InternalAlignment(g41,g42)
    c: InternalAlignment(g43,g42)
    c: InternalAlignment(g44,g42)
    c: Weight(g45) = 1
    c: Equal(g45,g46)
    c: Equal(g45,g47)
    c: InternalAlignment(g45,g48)
    c: InternalAlignment(g46,g48)
    c: InternalAlignment(g47,g48)
    c: InternalAlignment(g49,g48)
    c: InternalAlignment(g50,g48)
    c: Block(g42)
    c: Block(g48)
    c: Coincident(g51,g6)
    c: Coincident(g51,g5)
    c: Horizontal(g51)
    c: Distance(g51) = 450
    c: Coincident(g52,g6)
    c: Coincident(g52,g5)
    c: Horizontal(g52)
    c: Horizontal(g53)
    c: Coincident(g4,g53)
    c: Block(g53)
    c: Coincident(g1,g53)
    c: Weight(g54) = 1
    c: Equal(g54,g55)
    c: Equal(g54,g56)
    c: InternalAlignment(g54,g57)
    c: InternalAlignment(g55,g57)
    c: InternalAlignment(g56,g57)
    c: InternalAlignment(g58,g57)
    c: InternalAlignment(g59,g57)
    c: Block(g57)
    c: Weight(g60) = 1
    c: Equal(g60,g61)
    c: Equal(g60,g62)
    c: InternalAlignment(g60,g63)
    c: InternalAlignment(g61,g63)
    c: InternalAlignment(g62,g63)
    c: InternalAlignment(g64,g63)
    c: InternalAlignment(g65,g63)
    c: Block(g63)
    c: Weight(g66) = 1
    c: Equal(g66,g67)
    c: Equal(g66,g68)
    c: InternalAlignment(g66,g69)
    c: InternalAlignment(g67,g69)
    c: InternalAlignment(g68,g69)
    c: InternalAlignment(g70,g69)
    c: InternalAlignment(g71,g69)
    c: Block(g69)
    c: Weight(g72) = 1
    c: Equal(g72,g73)
    c: Equal(g72,g74)
    c: InternalAlignment(g72,g75)
    c: InternalAlignment(g73,g75)
    c: InternalAlignment(g74,g75)
    c: InternalAlignment(g76,g75)
    c: InternalAlignment(g77,g75)
    c: Block(g75)
    c: Weight(g78) = 1
    c: Equal(g78,g79)
    c: Equal(g78,g80)
    c: InternalAlignment(g78,g81)
    c: InternalAlignment(g79,g81)
    c: InternalAlignment(g80,g81)
    c: InternalAlignment(g82,g81)
    c: InternalAlignment(g83,g81)
    c: Weight(g84) = 1
    c: Equal(g84,g85)
    c: Equal(g84,g86)
    c: InternalAlignment(g84,g87)
    c: InternalAlignment(g85,g87)
    c: InternalAlignment(g86,g87)
    c: InternalAlignment(g88,g87)
    c: InternalAlignment(g89,g87)
    c: Block(g81)
    c: Block(g87)
    c: Coincident(g90,g81)
    c: Coincident(g90,g87)
    c: Vertical(g90)
    c: Coincident(g91,g81)
    c: Coincident(g91,g63)
    c: Coincident(g92,g63)
    c: Coincident(g92,g87)
    c: Weight(g93) = 1
    c: Equal(g93,g94)
    c: Equal(g93,g95)
    c: InternalAlignment(g93,g96)
    c: InternalAlignment(g94,g96)
    c: InternalAlignment(g95,g96)
    c: InternalAlignment(g97,g96)
    c: InternalAlignment(g98,g96)
    c: Weight(g99) = 1
    c: Equal(g99,g100)
    c: Equal(g99,g101)
    c: InternalAlignment(g99,g102)
    c: InternalAlignment(g100,g102)
    c: InternalAlignment(g101,g102)
    c: InternalAlignment(g103,g102)
    c: InternalAlignment(g104,g102)
    c: Block(g96)
    c: Block(g102)
    c: Coincident(g105,g96)
    c: Coincident(g105,g102)
    c: Vertical(g105)
    c: Coincident(g106,g96)
    c: Coincident(g106,g57)
    c: Coincident(g107,g57)
    c: Coincident(g107,g102)
    c: Weight(g108) = 1
    c: Equal(g108,g109)
    c: Equal(g108,g110)
    c: InternalAlignment(g108,g111)
    c: InternalAlignment(g109,g111)
    c: InternalAlignment(g110,g111)
    c: InternalAlignment(g112,g111)
    c: InternalAlignment(g113,g111)
    c: Weight(g114) = 1
    c: Equal(g114,g115)
    c: Equal(g114,g116)
    c: InternalAlignment(g114,g117)
    c: InternalAlignment(g115,g117)
    c: InternalAlignment(g116,g117)
    c: InternalAlignment(g118,g117)
    c: InternalAlignment(g119,g117)
    c: Block(g111)
    c: Block(g117)
    c: Coincident(g120,g111)
    c: Coincident(g120,g117)
    c: Vertical(g120)
    c: Coincident(g121,g117)
    c: Coincident(g121,g75)
    c: Coincident(g122,g75)
    c: Coincident(g122,g111)
    c: Weight(g123) = 1
    c: Equal(g123,g124)
    c: Equal(g123,g125)
    c: InternalAlignment(g123,g126)
    c: InternalAlignment(g124,g126)
    c: InternalAlignment(g125,g126)
    c: InternalAlignment(g127,g126)
    c: InternalAlignment(g128,g126)
    c: Weight(g129) = 1
    c: Equal(g129,g130)
    c: Equal(g129,g131)
    c: InternalAlignment(g129,g132)
    c: InternalAlignment(g130,g132)
    c: InternalAlignment(g131,g132)
    c: InternalAlignment(g133,g132)
    c: InternalAlignment(g134,g132)
    c: Block(g126)
    c: Block(g132)
    c: Coincident(g135,g126)
    c: Coincident(g135,g132)
    c: Vertical(g135)
    c: Coincident(g136,g132)
    c: Coincident(g136,g69)
    c: Coincident(g137,g69)
    c: Coincident(g137,g126)
    c: Weight(g138) = 1
    c: Equal(g138,g139)
    c: Equal(g138,g140)
    c: InternalAlignment(g138,g141)
    c: InternalAlignment(g139,g141)
    c: InternalAlignment(g140,g141)
    c: InternalAlignment(g142,g141)
    c: InternalAlignment(g143,g141)
    c: Weight(g144) = 1
    c: Equal(g144,g145)
    c: Equal(g144,g146)
    c: InternalAlignment(g144,g147)
    c: InternalAlignment(g145,g147)
    c: InternalAlignment(g146,g147)
    c: InternalAlignment(g148,g147)
    c: InternalAlignment(g149,g147)
    c: Weight(g150) = 1
    c: Equal(g150,g151)
    c: Equal(g150,g152)
    c: InternalAlignment(g150,g153)
    c: InternalAlignment(g151,g153)
    c: InternalAlignment(g152,g153)
    c: InternalAlignment(g154,g153)
    c: InternalAlignment(g155,g153)
    c: Weight(g156) = 1
    c: Equal(g156,g157)
    c: Equal(g156,g158)
    c: InternalAlignment(g156,g159)
    c: InternalAlignment(g157,g159)
    c: InternalAlignment(g158,g159)
    c: InternalAlignment(g160,g159)
    c: InternalAlignment(g161,g159)
    c: Block(g159)
    c: Block(g153)
    c: Block(g147)
    c: Block(g141)
    c: Coincident(g162,g36)
    c: Coincident(g162,g159)
    c: Coincident(g163,g159)
    c: Coincident(g163,g153)
    c: Horizontal(g163)
    c: Coincident(g164,g153)
    c: Coincident(g164,g36)
    c: Vertical(g164)
    c: Coincident(g165,g30)
    c: Coincident(g165,g147)
    c: Vertical(g165)
    c: Coincident(g166,g147)
    c: Coincident(g166,g141)
    c: Horizontal(g166)
    c: Coincident(g167,g141)
    c: Coincident(g167,g30)
    c: Weight(g168) = 1
    c: Equal(g168,g169)
    c: Equal(g168,g170)
    c: InternalAlignment(g168,g171)
    c: InternalAlignment(g169,g171)
    c: InternalAlignment(g170,g171)
    c: InternalAlignment(g172,g171)
    c: InternalAlignment(g173,g171)
    c: Weight(g174) = 1
    c: Equal(g174,g175)
    c: Equal(g174,g176)
    c: InternalAlignment(g174,g177)
    c: InternalAlignment(g175,g177)
    c: InternalAlignment(g176,g177)
    c: InternalAlignment(g178,g177)
    c: InternalAlignment(g179,g177)
    c: Weight(g180) = 1
    c: Equal(g180,g181)
    c: Equal(g180,g182)
    c: InternalAlignment(g180,g183)
    c: InternalAlignment(g181,g183)
    c: InternalAlignment(g182,g183)
    c: InternalAlignment(g184,g183)
    c: InternalAlignment(g185,g183)
    c: Weight(g186) = 1
    c: Equal(g186,g187)
    c: Equal(g186,g188)
    c: InternalAlignment(g186,g189)
    c: InternalAlignment(g187,g189)
    c: InternalAlignment(g188,g189)
    c: InternalAlignment(g190,g189)
    c: InternalAlignment(g191,g189)
    c: Block(g189)
    c: Block(g183)
    c: Block(g177)
    c: Block(g171)
    c: Coincident(g192,g189)
    c: Coincident(g192,g183)
    c: Horizontal(g192)
    c: Coincident(g193,g183)
    c: Coincident(g193,g18)
    c: Vertical(g193)
    c: Coincident(g194,g24)
    c: Coincident(g194,g177)
    c: Vertical(g194)
    c: Coincident(g195,g177)
    c: Coincident(g195,g171)
    c: Horizontal(g195)
    c: Coincident(g196,g171)
    c: Coincident(g196,g24)
    c: Coincident(g197,g18)
    c: Weight(g198) = 1
    c: Equal(g198,g199)
    c: Equal(g198,g200)
    c: InternalAlignment(g198,g201)
    c: InternalAlignment(g199,g201)
    c: InternalAlignment(g200,g201)
    c: InternalAlignment(g202,g201)
    c: InternalAlignment(g203,g201)
    c: Weight(g204) = 1
    c: Equal(g204,g205)
    c: Equal(g204,g206)
    c: InternalAlignment(g204,g207)
    c: InternalAlignment(g205,g207)
    c: InternalAlignment(g206,g207)
    c: InternalAlignment(g208,g207)
    c: InternalAlignment(g209,g207)
    c: Block(g207)
    c: Block(g201)
    c: Coincident(g210,g207)
    c: Coincident(g210,g42)
    c: Coincident(g211,g42)
    c: Coincident(g211,g201)
    c: Coincident(g212,g201)
    c: Coincident(g212,g207)
    c: Vertical(g212)
    c: Weight(g213) = 1
    c: Equal(g213,g214)
    c: Equal(g213,g215)
    c: InternalAlignment(g213,g216)
    c: InternalAlignment(g214,g216)
    c: InternalAlignment(g215,g216)
    c: InternalAlignment(g217,g216)
    c: InternalAlignment(g218,g216)
    c: Weight(g219) = 1
    c: Equal(g219,g220)
    c: Equal(g219,g221)
    c: InternalAlignment(g219,g222)
    c: InternalAlignment(g220,g222)
    c: InternalAlignment(g221,g222)
    c: InternalAlignment(g223,g222)
    c: InternalAlignment(g224,g222)
    c: Block(g222)
    c: Block(g216)
    c: Coincident(g225,g216)
    c: Coincident(g225,g48)
    c: Coincident(g226,g48)
    c: Coincident(g226,g222)
    c: Coincident(g227,g222)
    c: Coincident(g227,g216)
    c: Vertical(g227)
    c: Horizontal(g228)
    c: Block(g228)
    c: Vertical(g229)
    c: Block(g229)
    c: Block(g230)
    c: Weight(g231) = 1
    c: Equal(g231,g232)
    c: Equal(g231,g233)
    c: InternalAlignment(g231,g234)
    c: InternalAlignment(g232,g234)
    c: InternalAlignment(g233,g234)
    c: InternalAlignment(g235,g234)
    c: InternalAlignment(g236,g234)
    c: Weight(g237) = 1
    c: Equal(g237,g238)
    c: Equal(g237,g239)
    c: InternalAlignment(g237,g240)
    c: InternalAlignment(g238,g240)
    c: InternalAlignment(g239,g240)
    c: InternalAlignment(g241,g240)
    c: InternalAlignment(g242,g240)
    c: Weight(g243) = 1
    c: Equal(g243,g244)
    c: Equal(g243,g245)
    c: InternalAlignment(g243,g246)
    c: InternalAlignment(g244,g246)
    c: InternalAlignment(g245,g246)
    c: InternalAlignment(g247,g246)
    c: InternalAlignment(g248,g246)
    c: Weight(g249) = 1
    c: Equal(g249,g250)
    c: Equal(g249,g251)
    c: InternalAlignment(g249,g252)
    c: InternalAlignment(g250,g252)
    c: InternalAlignment(g251,g252)
    c: InternalAlignment(g253,g252)
    c: InternalAlignment(g254,g252)
    c: Block(g234)
    c: Block(g240)
    c: Block(g246)
    c: Block(g252)
    c: Coincident(g255,g240)
    c: Coincident(g255,g234)
    c: Horizontal(g255)
    c: Block(g197)
    c: Weight(g256) = 1
    c: Equal(g256,g257)
    c: Equal(g256,g258)
    c: InternalAlignment(g256,g259)
    c: InternalAlignment(g257,g259)
    c: InternalAlignment(g258,g259)
    c: InternalAlignment(g260,g259)
    c: InternalAlignment(g261,g259)
    c: Weight(g262) = 1
    c: Equal(g262,g263)
    c: Equal(g262,g264)
    c: InternalAlignment(g262,g265)
    c: InternalAlignment(g263,g265)
    c: InternalAlignment(g264,g265)
    c: InternalAlignment(g266,g265)
    c: InternalAlignment(g267,g265)
    c: Weight(g268) = 1
    c: Equal(g268,g269)
    c: Equal(g268,g270)
    c: InternalAlignment(g268,g271)
    c: InternalAlignment(g269,g271)
    c: InternalAlignment(g270,g271)
    c: InternalAlignment(g272,g271)
    c: InternalAlignment(g273,g271)
    c: Weight(g274) = 1
    c: Equal(g274,g275)
    c: Equal(g274,g276)
    c: InternalAlignment(g274,g277)
    c: InternalAlignment(g275,g277)
    c: InternalAlignment(g276,g277)
    c: InternalAlignment(g278,g277)
    c: InternalAlignment(g279,g277)
    c: Block(g259)
    c: Block(g265)
    c: Block(g271)
    c: Block(g277)
    c: Coincident(g280,g271)
    c: Coincident(g280,g277)
    c: Horizontal(g280)
    c: Coincident(g281,g277)
    c: Coincident(g281,g259)
    c: Vertical(g281)
    c: Coincident(g282,g259)
    c: Coincident(g282,g265)
    c: Coincident(g283,g265)
    c: Coincident(g283,g271)
    c: Vertical(g283)
    c: Weight(g284) = 1
    c: Equal(g284,g285)
    c: Equal(g284,g286)
    c: InternalAlignment(g284,g287)
    c: InternalAlignment(g285,g287)
    c: InternalAlignment(g286,g287)
    c: InternalAlignment(g288,g287)
    c: InternalAlignment(g289,g287)
    c: Weight(g290) = 1
    c: Equal(g290,g291)
    c: Equal(g290,g292)
    c: InternalAlignment(g290,g293)
    c: InternalAlignment(g291,g293)
    c: InternalAlignment(g292,g293)
    c: InternalAlignment(g294,g293)
    c: InternalAlignment(g295,g293)
    c: Weight(g296) = 1
    c: Equal(g296,g297)
    c: Equal(g296,g298)
    c: InternalAlignment(g296,g299)
    c: InternalAlignment(g297,g299)
    c: InternalAlignment(g298,g299)
    c: InternalAlignment(g300,g299)
    c: InternalAlignment(g301,g299)
    c: Block(g299)
    c: Block(g293)
    c: Block(g287)
    c: Coincident(g302,g293)
    c: Coincident(g302,g287)
    c: Coincident(g303,g287)
    c: Coincident(g303,g299)
    c: Vertical(g303)
    c: Coincident(g304,g299)
    c: Coincident(g304,g293)
    c: Horizontal(g304)
    c: Weight(g305) = 1
    c: Equal(g305,g306)
    c: InternalAlignment(g305,g307)
    c: InternalAlignment(g306,g307)
    c: InternalAlignment(g308,g307)
    c: InternalAlignment(g309,g307)
    c: Weight(g310) = 1
    c: Equal(g310,g311)
    c: Equal(g310,g312)
    c: InternalAlignment(g310,g313)
    c: InternalAlignment(g311,g313)
    c: InternalAlignment(g312,g313)
    c: InternalAlignment(g314,g313)
    c: InternalAlignment(g315,g313)
    c: Weight(g316) = 1
    c: Equal(g316,g317)
    c: Equal(g316,g318)
    c: InternalAlignment(g316,g319)
    c: InternalAlignment(g317,g319)
    c: InternalAlignment(g318,g319)
    c: InternalAlignment(g320,g319)
    c: InternalAlignment(g321,g319)
    c: Equal(g322,g323)
    c: Equal(g322,g324)
    c: InternalAlignment(g322,g325)
    c: InternalAlignment(g323,g325)
    c: InternalAlignment(g324,g325)
    c: InternalAlignment(g326,g325)
    c: InternalAlignment(g327,g325)
    c: Block(g313)
    c: Block(g319)
    c: Block(g325)
    c: Block(g307)
    c: Coincident(g328,g307)
    c: Coincident(g328,g313)
    c: Horizontal(g328)
    c: Coincident(g329,g313)
    c: Coincident(g329,g319)
    c: Vertical(g329)
    c: Coincident(g330,g319)
    c: Coincident(g330,g325)
    c: Horizontal(g330)
    c: Coincident(g331,g325)
    c: Coincident(g331,g307)
    c: Vertical(g332)
    c: Vertical(g333)
    c: Horizontal(g334)
    c: Horizontal(g335)
    c: Distance(g335) = 4
    c: Distance(g334) = 4
    c: Distance(g336) = 4
    c: Distance(g337) = 4
    c: Distance(g332) = 4
    c: Distance(g333) = 4
    c: Parallel(g2,g337)
    c: Parallel(g336,g2)
    c: Coincident(g333,g3)
    c: Coincident(g334,g3)
    c: Coincident(g335,g2)
    c: Coincident(g332,g2)
    c: Coincident(g337,g2)
FEATURE [Sketcher::SketchObject] Sketch001
  FullyConstrained = true
  MapMode = 4
  Placement = pos=(0,0,0) rot=(0.57735,0.57735,0.57735;2.0944rad)
  Support = -> [Sketch]
  sketch-geometry (46):
    g0: BSplineCurve PolesCount=3 KnotsCount=2 Degree=2 IsPeriodic=0
    g1: ArcOfCircle CenterX=73.1223 CenterY=-32.291 CenterZ=0 NormalX=0 NormalY=0 NormalZ=1 AngleXU=0 Radius=13 StartAngle=5.92268 EndAngle=9.06428
    g2: ArcOfCircle CenterX=66.7816 CenterY=-49.1439 CenterZ=0 NormalX=0 NormalY=0 NormalZ=1 AngleXU=0 Radius=13 StartAngle=2.78068 EndAngle=5.92131
    g3: ArcOfCircle CenterX=55.9263 CenterY=-78.1807 CenterZ=0 NormalX=0 NormalY=0 NormalZ=1 AngleXU=0 Radius=13 StartAngle=5.92268 EndAngle=9.06428
    g4: ArcOfCircle CenterX=49.5884 CenterY=-95.0342 CenterZ=0 NormalX=0 NormalY=0 NormalZ=1 AngleXU=0 Radius=13 StartAngle=2.78068 EndAngle=5.92131
    g5: ArcOfCircle CenterX=38.7206 CenterY=-124.067 CenterZ=0 NormalX=0 NormalY=0 NormalZ=1 AngleXU=0 Radius=13 StartAngle=5.92268 EndAngle=9.06428
    g6: ArcOfCircle CenterX=32.3875 CenterY=-140.92 CenterZ=0 NormalX=0 NormalY=0 NormalZ=1 AngleXU=0 Radius=13 StartAngle=2.78068 EndAngle=5.92131
    g7: ArcOfCircle CenterX=21.4715 CenterY=-169.934 CenterZ=0 NormalX=0 NormalY=0 NormalZ=1 AngleXU=0 Radius=13 StartAngle=5.92268 EndAngle=9.06428
    g8: ArcOfCircle CenterX=15.1336 CenterY=-186.787 CenterZ=0 NormalX=0 NormalY=0 NormalZ=1 AngleXU=0 Radius=13 StartAngle=2.78068 EndAngle=5.92131
    g9-g12: Circle x4 (B-spline internal-alignment scaffolding for g13; pole/knot coordinates omitted)
    g13: BSplineCurve PolesCount=4 KnotsCount=2 Degree=3 IsPeriodic=0
    g14: GeomPoint X=28.8094 Y=-19.0875 Z=0
    g15: GeomPoint X=47.0443 Y=-50.4712 Z=0
    g16: Circle CenterX=53.5586 CenterY=-23.2695 CenterZ=0 NormalX=0 NormalY=0 NormalZ=1 AngleXU=0 Radius=3.24518
    g17: Circle CenterX=-195.441 CenterY=-127.082 CenterZ=0 NormalX=0 NormalY=0 NormalZ=1 AngleXU=0 Radius=1
    g18: Circle CenterX=-8.24091 CenterY=-197.481 CenterZ=0 NormalX=0 NormalY=0 NormalZ=1 AngleXU=0 Radius=1
    g19: Circle CenterX=12.8789 CenterY=-141.321 CenterZ=0 NormalX=0 NormalY=0 NormalZ=1 AngleXU=0 Radius=1
    g20: BSplineCurve PolesCount=3 KnotsCount=2 Degree=2 IsPeriodic=0
    g21: GeomPoint X=-195.441 Y=-127.082 Z=0
    g22: GeomPoint X=12.8789 Y=-141.321 Z=0
    g23: Circle CenterX=-12.8016 CenterY=-179.036 CenterZ=0 NormalX=0 NormalY=0 NormalZ=1 AngleXU=0 Radius=10.5072
    g24: Circle CenterX=0.933922 CenterY=-166.43 CenterZ=0 NormalX=0 NormalY=0 NormalZ=1 AngleXU=0 Radius=3.26661
    g25: Circle CenterX=-33.5518 CenterY=-176.44 CenterZ=0 NormalX=0 NormalY=0 NormalZ=1 AngleXU=0 Radius=5.64388
    g26: Circle CenterX=-47.2366 CenterY=-173.859 CenterZ=0 NormalX=0 NormalY=0 NormalZ=1 AngleXU=0 Radius=3.01653
    g27: Circle CenterX=-56.2595 CenterY=-171.456 CenterZ=0 NormalX=0 NormalY=0 NormalZ=1 AngleXU=0 Radius=2.12826
    g28: ArcOfCircle CenterX=51.2151 CenterY=-198.473 CenterZ=0 NormalX=0 NormalY=0 NormalZ=1 AngleXU=0 Radius=20 StartAngle=2.78189 EndAngle=4.35269
    g29: LineSegment StartX=32.4951 StartY=-191.433 StartZ=0 EndX=94.6578 EndY=-26.1352 EndZ=0
    g30: LineSegment StartX=43.1192 StartY=-220.001 StartZ=0 EndX=-196.497 EndY=-129.89 EndZ=0
    g31: LineSegment StartX=43.1192 StartY=-220.001 StartZ=0 EndX=44.1752 EndY=-217.193 EndZ=0
    g32: LineSegment StartX=117.223 StartY=-19.0875 StartZ=0 EndX=117.223 EndY=-16.0875 EndZ=0
    g33: LineSegment StartX=117.223 StartY=-16.0875 StartZ=0 EndX=17.2232 EndY=-16.0875 EndZ=0
    g34: LineSegment StartX=17.2232 StartY=-16.0875 StartZ=0 EndX=17.2232 EndY=-19.0875 EndZ=0
    g35: LineSegment StartX=28.8094 StartY=-19.0875 StartZ=0 EndX=17.2232 EndY=-19.0875 EndZ=0
    g36: LineSegment StartX=47.0443 StartY=-50.4712 StartZ=0 EndX=12.8789 EndY=-141.321 EndZ=0
    g37: LineSegment StartX=-195.441 StartY=-127.082 StartZ=0 EndX=-196.497 EndY=-129.89 EndZ=0
    g38: LineSegment StartX=85.2866 StartY=-36.8766 StartZ=0 EndX=78.9396 EndY=-53.7463 EndZ=0
    g39: LineSegment StartX=60.9579 StartY=-27.7053 StartZ=0 EndX=54.6191 EndY=-44.5532 EndZ=0
    g40: LineSegment StartX=68.0907 StartY=-82.7664 StartZ=0 EndX=61.7465 EndY=-99.6365 EndZ=0
    g41: LineSegment StartX=43.7619 StartY=-73.595 StartZ=0 EndX=37.426 EndY=-90.4435 EndZ=0
    g42: LineSegment StartX=50.885 StartY=-128.652 StartZ=0 EndX=44.5456 EndY=-145.522 EndZ=0
    g43: LineSegment StartX=26.5562 StartY=-119.481 StartZ=0 EndX=20.2251 EndY=-136.329 EndZ=0
    g44: LineSegment StartX=9.3071 StartY=-165.349 StartZ=0 EndX=2.97115 EndY=-182.197 EndZ=0
    g45: LineSegment StartX=33.6358 StartY=-174.52 StartZ=0 EndX=27.2917 EndY=-191.39 EndZ=0
  constraints (71):
    c: Block(g0)
    c: Block(g1)
    c: Block(g2)
    c: Block(g4)
    c: Block(g3)
    c: Block(g6)
    c: Block(g5)
    c: Block(g8)
    c: Block(g7)
    c: Weight(g9) = 1
    c: Equal(g9,g10)
    c: Equal(g9,g11)
    c: Equal(g9,g12)
    c: InternalAlignment(g9-g12 -> g13) x4
    c: InternalAlignment(g14,g13)
    c: InternalAlignment(g15,g13)
    c: Block(g16)
    c: Weight(g17) = 1
    c: Equal(g17,g18)
    c: Equal(g17,g19)
    c: InternalAlignment(g17,g20)
    c: InternalAlignment(g18,g20)
    c: InternalAlignment(g19,g20)
    c: InternalAlignment(g21,g20)
    c: InternalAlignment(g22,g20)
    c: Block(g20)
    c: Block(g23)
    c: Block(g24)
    c: Block(g25)
    c: Block(g26)
    c: Block(g27)
    c: Block(g28)
    c: Coincident(g29,g28)
    c: Coincident(g29,g0)
    c: Block(g13)
    c: Coincident(g31,g30)
    c: Coincident(g31,g28)
    c: Block(g31)
    c: Coincident(g32,g0)
    c: Vertical(g32)
    c: Coincident(g33,g32)
    c: Horizontal(g33)
    c: Coincident(g34,g33)
    c: Vertical(g34)
    c: Block(g33)
    c: Coincident(g35,g13)
    c: Coincident(g35,g34)
    c: Horizontal(g35)
    c: Coincident(g36,g13)
    c: Coincident(g36,g20)
    c: Coincident(g37,g20)
    c: Coincident(g37,g30)
    c: Block(g30)
    c: Coincident(g38,g1)
    c: Coincident(g38,g2)
    c: Coincident(g39,g1)
    c: Coincident(g39,g2)
    c: Coincident(g40,g3)
    c: Coincident(g40,g4)
    c: Coincident(g41,g3)
    c: Coincident(g41,g4)
    c: Coincident(g42,g5)
    c: Coincident(g42,g6)
    c: Coincident(g43,g5)
    c: Coincident(g43,g6)
    c: Coincident(g44,g7)
    c: Coincident(g44,g8)
    c: Coincident(g45,g7)
    c: Coincident(g45,g8)
    c: Distance(g30) = 256
    c: Distance(g33) = 100
FEATURE [Part::Extrusion] Extrude002
  Base = -> Sketch001
  Dir = (1,0,0)
  DirMode = 2
  FaceMakerClass = Part::FaceMakerBullseye
  LengthFwd = 8
  LengthRev = 0
  Solid = true
  Symmetric = false
FEATURE [Sketcher::SketchObject] Sketch002
  FullyConstrained = true
  sketch-geometry (20):
    g0: LineSegment StartX=-2.77179 StartY=-200.304 StartZ=0 EndX=5.22821 EndY=-200.304 EndZ=0
    g1: LineSegment StartX=5.22821 StartY=-200.304 StartZ=0 EndX=5.22821 EndY=-197.304 EndZ=0
    g2: LineSegment StartX=-2.77179 StartY=-200.304 StartZ=0 EndX=-2.77179 EndY=-197.304 EndZ=0
    g3: LineSegment StartX=5.22821 StartY=-197.304 StartZ=0 EndX=8.22821 EndY=-197.304 EndZ=0
    g4: LineSegment StartX=-2.77179 StartY=-197.304 StartZ=0 EndX=-5.77179 EndY=-197.304 EndZ=0
    g5: LineSegment StartX=19.2282 StartY=-203.304 StartZ=0 EndX=19.2282 EndY=-206.304 EndZ=0
    g6: LineSegment StartX=-16.7718 StartY=-203.304 StartZ=0 EndX=-16.7718 EndY=-206.304 EndZ=0
    g7: LineSegment StartX=-16.7718 StartY=-206.304 StartZ=0 EndX=19.2282 EndY=-206.304 EndZ=0
    g8: Circle CenterX=-16.7718 CenterY=-203.304 CenterZ=0 NormalX=0 NormalY=0 NormalZ=1 AngleXU=0 Radius=1
    g9: Circle CenterX=-5.77179 CenterY=-203.304 CenterZ=0 NormalX=0 NormalY=0 NormalZ=1 AngleXU=0 Radius=1
    g10: Circle CenterX=-5.77179 CenterY=-197.304 CenterZ=0 NormalX=0 NormalY=0 NormalZ=1 AngleXU=0 Radius=1
    g11: BSplineCurve PolesCount=3 KnotsCount=2 Degree=2 IsPeriodic=0
    g12: GeomPoint X=-16.7718 Y=-203.304 Z=0
    g13: GeomPoint X=-5.77179 Y=-197.304 Z=0
    g14: Circle CenterX=19.2282 CenterY=-203.304 CenterZ=0 NormalX=0 NormalY=0 NormalZ=1 AngleXU=0 Radius=1
    g15: Circle CenterX=8.22821 CenterY=-203.304 CenterZ=0 NormalX=0 NormalY=0 NormalZ=1 AngleXU=0 Radius=1
    g16: Circle CenterX=8.22821 CenterY=-197.304 CenterZ=0 NormalX=0 NormalY=0 NormalZ=1 AngleXU=0 Radius=1
    g17: BSplineCurve PolesCount=3 KnotsCount=2 Degree=2 IsPeriodic=0
    g18: GeomPoint X=19.2282 Y=-203.304 Z=0
    g19: GeomPoint X=8.22821 Y=-197.304 Z=0
  constraints (41):
    c: Horizontal(g0)
    c: Distance(g0) = 8
    c: Coincident(g1,g0)
    c: Vertical(g1)
    c: Distance(g1) = 3
    c: Coincident(g2,g0)
    c: Vertical(g2)
    c: Distance(g2) = 3
    c: Coincident(g3,g1)
    c: Horizontal(g3)
    c: Distance(g3) = 3
    c: Coincident(g4,g2)
    c: Horizontal(g4)
    c: Distance(g4) = 3
    c: Vertical(g5)
    c: Vertical(g6)
    c: Coincident(g7,g6)
    c: Coincident(g7,g5)
    c: Weight(g8) = 1
    c: Equal(g8,g9)
    c: Equal(g8,g10)
    c: Coincident(g11,g4)
    c: InternalAlignment(g8,g11)
    c: InternalAlignment(g9,g11)
    c: InternalAlignment(g10,g11)
    c: InternalAlignment(g12,g11)
    c: InternalAlignment(g13,g11)
    c: Coincident(g17,g5)
    c: Weight(g14) = 1
    c: Equal(g14,g15)
    c: Equal(g14,g16)
    c: Coincident(g17,g3)
    c: InternalAlignment(g14,g17)
    c: InternalAlignment(g15,g17)
    c: InternalAlignment(g16,g17)
    c: InternalAlignment(g18,g17)
    c: InternalAlignment(g19,g17)
    c: Block(g7)
    c: Block(g17)
    c: Block(g11)
    c: Block(g6)
FEATURE [Part::Extrusion] Extrude003
  Base = -> Sketch002
  Dir = (0,0,1)
  DirMode = 2
  FaceMakerClass = Part::FaceMakerBullseye
  LengthFwd = 260
  LengthRev = 0
  Solid = true
  Symmetric = false
FEATURE [Part::Extrusion] Extrude
  Base = -> Sketch
  Dir = (0,0,1)
  DirMode = 2
  FaceMakerClass = Part::FaceMakerBullseye
  LengthFwd = 14
  LengthRev = 0
  Solid = true
  Symmetric = false
